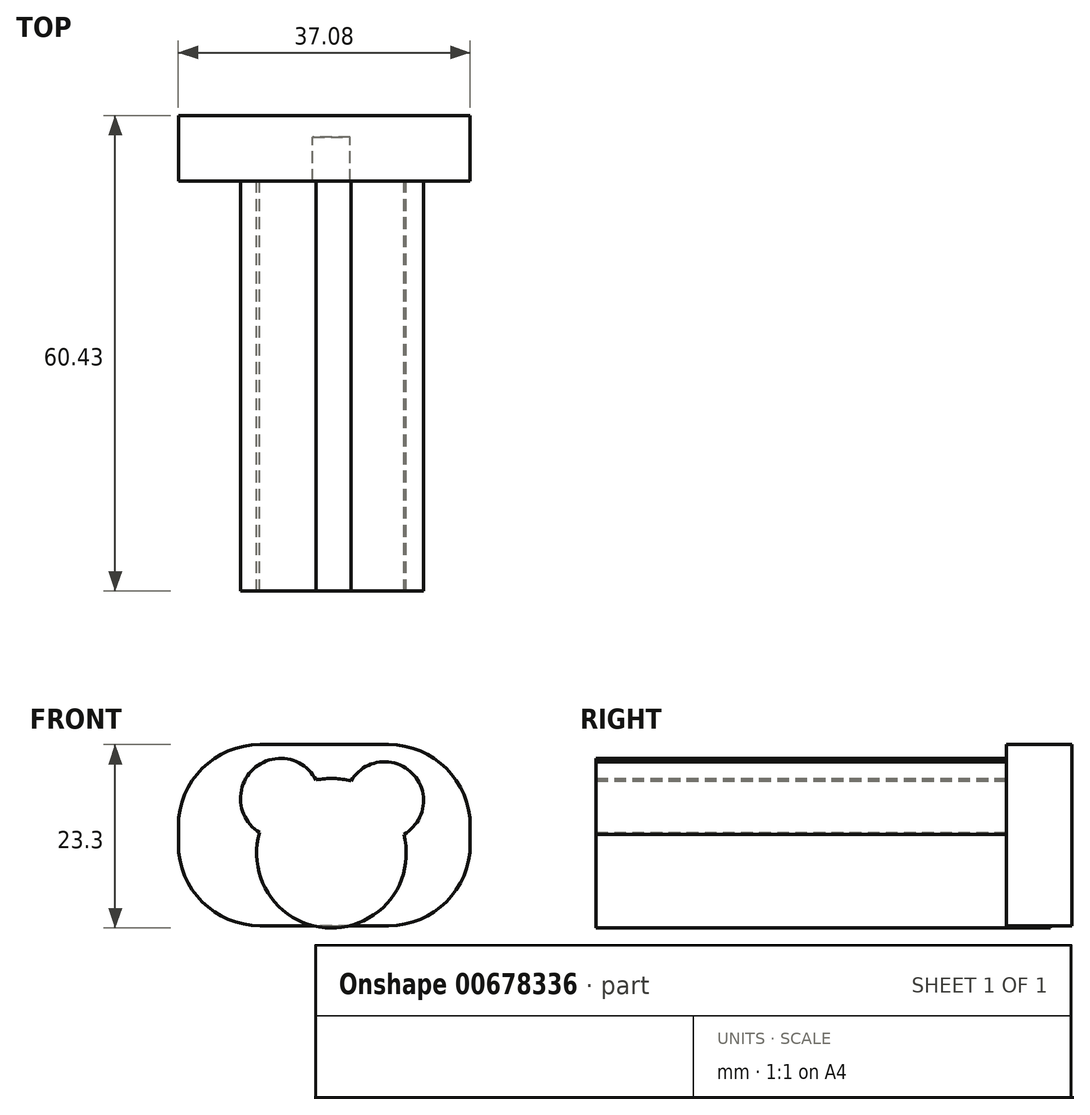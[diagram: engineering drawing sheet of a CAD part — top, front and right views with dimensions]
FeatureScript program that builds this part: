
annotation { "Feature Type Name" : "Feature", "Feature Type Description" : "" }
export const myFeature = defineFeature(function(context is Context, id is Id, definition is map)
    precondition{}
    {
        {
            var Q0;
            Q0=qCreatedBy(makeId("Front.planeOp"),FACE);
            var sketch = newSketch(context, id + "F0", { "sketchPlane" : qUnion([Q0])});
            skCircle(sketch, "E0", {"center": v(0.62, -4.7) * mm, "radius": 9.5 * mm});
            skCircle(sketch, "E1", {"center": v(-5.84, 2.27) * mm, "radius": 5.08 * mm});
            skCircle(sketch, "E2", {"center": v(7.38, 2) * mm, "radius": 4.94 * mm});
            skSolve(sketch);
        }
        {
            var Q0;
            {var subQ0=sQuery(id+"F0.wireOp",EDGE,"E2");var subQ1=sQuery(id+"F0.wireOp",EDGE,"E0");var subQ2=makeQuery(id+"F0.imprint","INTERSECT",VERTEX,{"disambiguationData":[OD(0.0)],"derivedFrom":[subQ1,subQ0]});Q0=makeQuery(id+"F0.imprint","IMPRINT",FACE,{"disambiguationData":[TD([[makeQuery(id+"F0.imprint","IMPRINT",EDGE,{"disambiguationData":[TD([[subQ2,-1.0]])],"derivedFrom":subQ1}),1.0]])]});}
            var Q1;
            {var subQ0=sQuery(id+"F0.wireOp",EDGE,"E1");var subQ1=sQuery(id+"F0.wireOp",EDGE,"E0");var subQ2=makeQuery(id+"F0.imprint","INTERSECT",VERTEX,{"disambiguationData":[OD(0.0)],"derivedFrom":[subQ1,subQ0]});Q1=makeQuery(id+"F0.imprint","IMPRINT",FACE,{"disambiguationData":[TD([[makeQuery(id+"F0.imprint","IMPRINT",EDGE,{"disambiguationData":[TD([[subQ2,-1.0]])],"derivedFrom":subQ1}),1.0]])]});}
            var Q2;
            {var subQ0=sQuery(id+"F0.wireOp",EDGE,"E2");var subQ1=sQuery(id+"F0.wireOp",EDGE,"E0");var subQ2=makeQuery(id+"F0.imprint","INTERSECT",VERTEX,{"disambiguationData":[OD(0.0)],"derivedFrom":[subQ1,subQ0]});Q2=makeQuery(id+"F0.imprint","IMPRINT",FACE,{"disambiguationData":[TD([[makeQuery(id+"F0.imprint","IMPRINT",EDGE,{"disambiguationData":[TD([[subQ2,1.0]])],"derivedFrom":subQ1}),1.0]])]});}
            var Q3;
            {var subQ0=sQuery(id+"F0.wireOp",EDGE,"E2");var subQ1=sQuery(id+"F0.wireOp",EDGE,"E0");var subQ2=makeQuery(id+"F0.imprint","INTERSECT",VERTEX,{"disambiguationData":[OD(0.0)],"derivedFrom":[subQ1,subQ0]});Q3=makeQuery(id+"F0.imprint","IMPRINT",FACE,{"disambiguationData":[TD([[makeQuery(id+"F0.imprint","IMPRINT",EDGE,{"disambiguationData":[TD([[subQ2,1.0]])],"derivedFrom":subQ1}),-1.0]])]});}
            var Q4;
            {var subQ0=sQuery(id+"F0.wireOp",EDGE,"E1");var subQ1=sQuery(id+"F0.wireOp",EDGE,"E0");var subQ2=makeQuery(id+"F0.imprint","INTERSECT",VERTEX,{"disambiguationData":[OD(0.0)],"derivedFrom":[subQ1,subQ0]});Q4=makeQuery(id+"F0.imprint","IMPRINT",FACE,{"disambiguationData":[TD([[makeQuery(id+"F0.imprint","IMPRINT",EDGE,{"disambiguationData":[TD([[subQ2,-1.0]])],"derivedFrom":subQ1}),-1.0]])]});}
            extrude(context, id + "F1", {"entities" : qUnion([Q0, Q1, Q2, Q3, Q4]), "depth" : 57.7 * mm, "offsetDistance" : 25 * mm});
        }
        {
            var Q0;
            Q0=qCreatedBy(makeId("Top.planeOp"),FACE);
            var sketch = newSketch(context, id + "F2", { "sketchPlane" : qUnion([Q0])});
            skLineSegment(sketch, "E3.bottom", {"start": v(-18.83, 2.73) * mm, "end": v(18.25, 2.73) * mm});
            skLineSegment(sketch, "E3.top", {"start": v(-18.83, -5.6) * mm, "end": v(18.25, -5.6) * mm});
            skLineSegment(sketch, "E3.left", {"start": v(-18.83, 2.73) * mm, "end": v(-18.83, -5.6) * mm});
            skLineSegment(sketch, "E3.right", {"start": v(18.25, 2.73) * mm, "end": v(18.25, -5.6) * mm});
            skSolve(sketch);
        }
        {
            var Q0;
            Q0=makeQuery(id+"F2.imprint","IMPRINT",FACE,{"disambiguationData":[TD([[makeQuery(id+"F2.imprint","IMPRINT",EDGE,{"derivedFrom":sQuery(id+"F2.wireOp",EDGE,"E3.bottom")}),-1.0]])]});
            extrude(context, id + "F3", {"entities" : qUnion([Q0]), "operationType" : NewBodyOperationType.ADD, "depth" : 9.1 * mm, "offsetDistance" : 25 * mm, "hasSecondDirection" : true, "secondDirectionOppositeDirection" : true, "secondDirectionDepth" : 13.9 * mm});
        }
        {
            var Q0;
            Q0=makeQuery(id+"F3.opExtrude","CAP_EDGE",EDGE,{"disambiguationData":[OSD([sQuery(id+"F2.wireOp",EDGE,"E3.left")])],"isStart":true});
            var Q1;
            Q1=makeQuery(id+"F3.opExtrude","CAP_EDGE",EDGE,{"disambiguationData":[OSD([sQuery(id+"F2.wireOp",EDGE,"E3.left")])],"isStart":false});
            var Q2;
            Q2=makeQuery(id+"F3.opExtrude","CAP_EDGE",EDGE,{"disambiguationData":[OSD([sQuery(id+"F2.wireOp",EDGE,"E3.right")])],"isStart":false});
            var Q3;
            Q3=makeQuery(id+"F3.opExtrude","CAP_EDGE",EDGE,{"disambiguationData":[OSD([sQuery(id+"F2.wireOp",EDGE,"E3.right")])],"isStart":true});
            fillet(context, id + "F4", {"entities" : qUnion([Q0, Q1, Q2, Q3]), "radius" : 10.38 * mm, "tangentPropagation" : true, "allowEdgeOverflow" : false});
        }
    });
